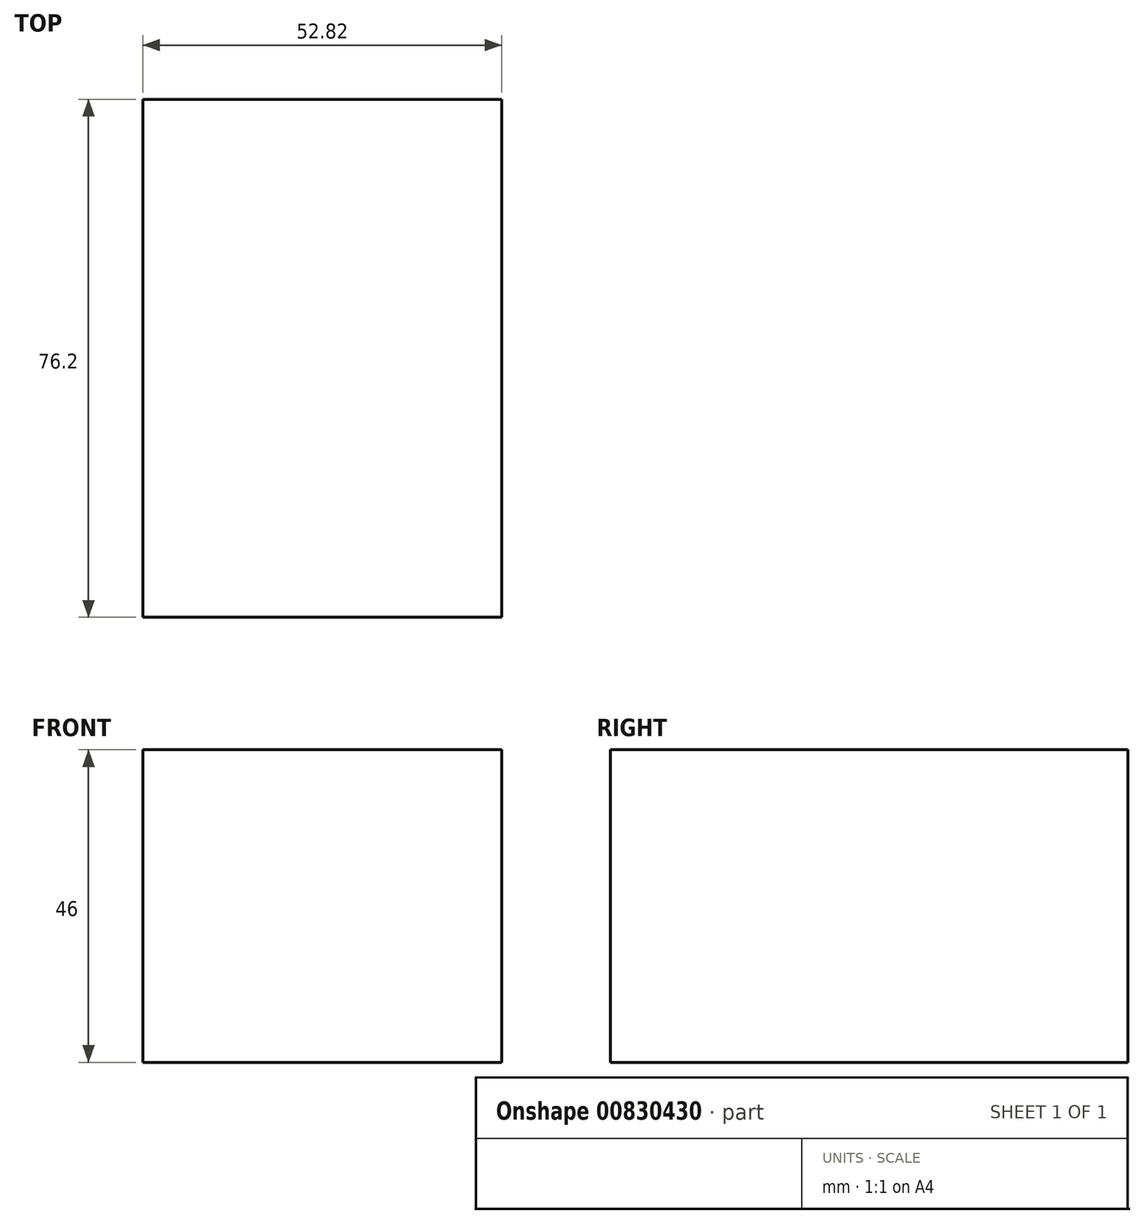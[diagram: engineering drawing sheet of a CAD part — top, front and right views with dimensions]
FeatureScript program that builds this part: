
annotation { "Feature Type Name" : "Feature", "Feature Type Description" : "" }
export const myFeature = defineFeature(function(context is Context, id is Id, definition is map)
    precondition{}
    {
        {
            var Q0;
            Q0=qCreatedBy(makeId("Front.planeOp"),FACE);
            var sketch = newSketch(context, id + "F0", { "sketchPlane" : qUnion([Q0])});
            skLineSegment(sketch, "E0.bottom", {"start": v(0, 0) * mm, "end": v(52.82, 0) * mm});
            skLineSegment(sketch, "E0.top", {"start": v(0, 46) * mm, "end": v(52.82, 46) * mm});
            skLineSegment(sketch, "E0.left", {"start": v(0, 0) * mm, "end": v(0, 46) * mm});
            skLineSegment(sketch, "E0.right", {"start": v(52.82, 0) * mm, "end": v(52.82, 46) * mm});
            skSolve(sketch);
        }
        {
            var Q0;
            Q0=makeQuery(id+"F0.imprint","IMPRINT",FACE,{"disambiguationData":[TD([[makeQuery(id+"F0.imprint","IMPRINT",EDGE,{"derivedFrom":sQuery(id+"F0.wireOp",EDGE,"E0.bottom")}),1.0]])]});
            extrude(context, id + "F1", {"entities" : qUnion([Q0]), "depth" : 76.2 * mm, "offsetDistance" : 25.4 * mm});
        }
    });
